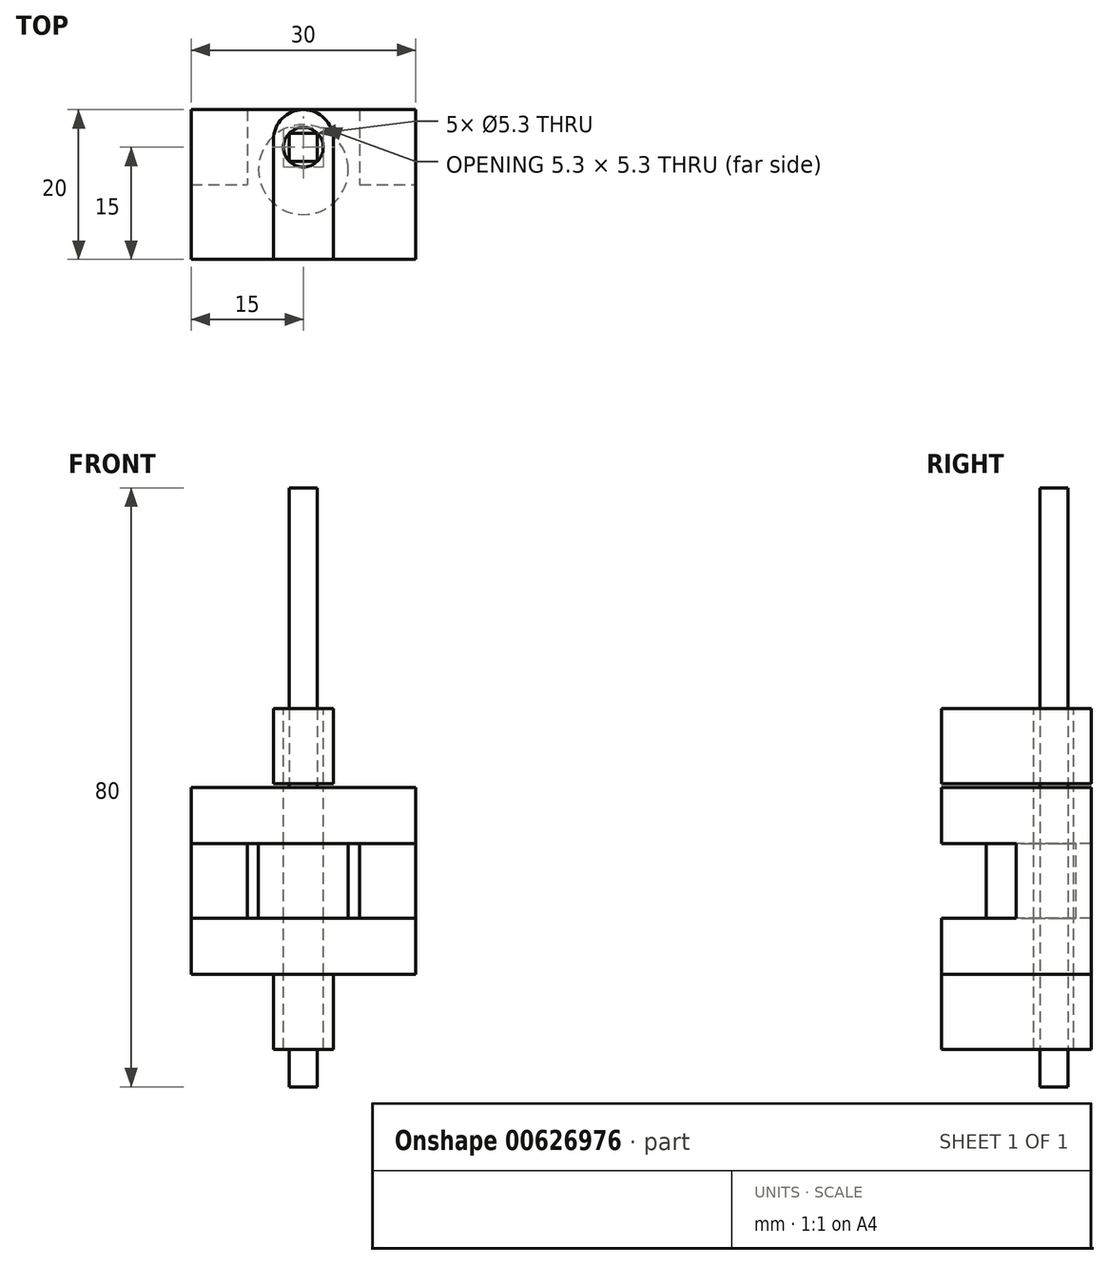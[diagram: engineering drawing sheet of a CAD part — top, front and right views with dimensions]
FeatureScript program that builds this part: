
annotation { "Feature Type Name" : "Feature", "Feature Type Description" : "" }
export const myFeature = defineFeature(function(context is Context, id is Id, definition is map)
    precondition{}
    {
        {
            var Q0;
            Q0=qCreatedBy(makeId("Top.planeOp"),FACE);
            var sketch = newSketch(context, id + "F0", { "sketchPlane" : qUnion([Q0])});
            skLineSegment(sketch, "E0.bottom", {"start": v(0, 0) * mm, "end": v(30, 0) * mm});
            skLineSegment(sketch, "E0.top", {"start": v(0, 20) * mm, "end": v(30, 20) * mm});
            skLineSegment(sketch, "E0.left", {"start": v(0, 0) * mm, "end": v(0, 20) * mm});
            skLineSegment(sketch, "E0.right", {"start": v(30, 0) * mm, "end": v(30, 20) * mm});
            skSolve(sketch);
        }
        {
            var Q0;
            Q0=makeQuery(id+"F0.imprint","IMPRINT",FACE,{"disambiguationData":[TD([[makeQuery(id+"F0.imprint","IMPRINT",EDGE,{"derivedFrom":sQuery(id+"F0.wireOp",EDGE,"E0.bottom")}),1.0]])]});
            extrude(context, id + "F1", {"entities" : qUnion([Q0]), "depth" : 25 * mm, "offsetDistance" : 25 * mm});
        }
        {
            var Q0;
            Q0=makeQuery(id+"F1.opExtrude","SWEPT_FACE",FACE,{"disambiguationData":[OSD([sQuery(id+"F0.wireOp",EDGE,"E0.bottom")])]});
            var sketch = newSketch(context, id + "F2", { "sketchPlane" : qUnion([Q0])});
            skLineSegment(sketch, "E1.bottom", {"start": v(0, 7.5) * mm, "end": v(30, 7.5) * mm});
            skLineSegment(sketch, "E1.top", {"start": v(0, 17.5) * mm, "end": v(30, 17.5) * mm});
            skLineSegment(sketch, "E1.left", {"start": v(0, 7.5) * mm, "end": v(0, 17.5) * mm});
            skLineSegment(sketch, "E1.right", {"start": v(30, 7.5) * mm, "end": v(30, 17.5) * mm});
            skLineSegment(sketch, "E2", {"start": v(20.4, 12.5) * mm, "end": v(0, 12.5) * mm, "construction": true});
            skSolve(sketch);
        }
        {
            var Q0;
            Q0=makeQuery(id+"F2.imprint","IMPRINT",FACE,{"disambiguationData":[TD([[makeQuery(id+"F2.imprint","IMPRINT",EDGE,{"derivedFrom":sQuery(id+"F2.wireOp",EDGE,"E1.bottom")}),1.0]])]});
            extrude(context, id + "F3", {"entities" : qUnion([Q0]), "operationType" : NewBodyOperationType.REMOVE, "oppositeDirection" : true, "depth" : 10 * mm, "offsetDistance" : 25 * mm});
        }
        {
            var Q0;
            Q0=makeQuery(id+"F3.boolean.opBoolean","COPY",FACE,{"derivedFrom":makeQuery(id+"F3.opExtrude","CAP_FACE",FACE,{"disambiguationData":[OSD([sQuery(id+"F2.wireOp",EDGE,"E1.bottom"),sQuery(id+"F2.wireOp",EDGE,"E1.top"),sQuery(id+"F2.wireOp",EDGE,"E1.left"),sQuery(id+"F2.wireOp",EDGE,"E1.right")])],"isStart":false})});
            var sketch = newSketch(context, id + "F4", { "sketchPlane" : qUnion([Q0])});
            skLineSegment(sketch, "E3.bottom", {"start": v(22.5, 17.5) * mm, "end": v(7.5, 17.5) * mm});
            skLineSegment(sketch, "E3.top", {"start": v(22.5, 7.5) * mm, "end": v(7.5, 7.5) * mm});
            skLineSegment(sketch, "E3.left", {"start": v(22.5, 17.5) * mm, "end": v(22.5, 7.5) * mm});
            skLineSegment(sketch, "E3.right", {"start": v(7.5, 17.5) * mm, "end": v(7.5, 7.5) * mm});
            skLineSegment(sketch, "E4", {"start": v(15, 17.5) * mm, "end": v(15, 7.5) * mm, "construction": true});
            skSolve(sketch);
        }
        {
            var Q0;
            Q0=makeQuery(id+"F4.imprint","IMPRINT",FACE,{"disambiguationData":[TD([[makeQuery(id+"F4.imprint","IMPRINT",EDGE,{"derivedFrom":sQuery(id+"F4.wireOp",EDGE,"E3.bottom")}),-1.0]])]});
            extrude(context, id + "F5", {"entities" : qUnion([Q0]), "operationType" : NewBodyOperationType.REMOVE, "endBound" : BoundingType.THROUGH_ALL, "oppositeDirection" : true, "depth" : 25 * mm, "offsetDistance" : 25 * mm});
        }
        {
            var Q0;
            Q0=makeQuery(id+"F5.boolean.opBoolean","MERGE",FACE,{"derivedFrom":[makeQuery(id+"F3.boolean.opBoolean","COPY",FACE,{"derivedFrom":makeQuery(id+"F3.opExtrude","SWEPT_FACE",FACE,{"disambiguationData":[OSD([sQuery(id+"F2.wireOp",EDGE,"E1.bottom")])]})}),makeQuery(id+"F5.opExtrude","SWEPT_FACE",FACE,{"disambiguationData":[OSD([sQuery(id+"F4.wireOp",EDGE,"E3.top")])]})]});
            var sketch = newSketch(context, id + "F6", { "sketchPlane" : qUnion([Q0])});
            skCircle(sketch, "E5", {"center": v(15, 15) * mm, "radius": 2.65 * mm});
            skLineSegment(sketch, "E6", {"start": v(15, 15) * mm, "end": v(15, 12.34) * mm, "construction": true});
            skSolve(sketch);
        }
        {
            var Q0;
            Q0=makeQuery(id+"F6.imprint","IMPRINT",FACE,{"disambiguationData":[TD([[makeQuery(id+"F6.imprint","IMPRINT",EDGE,{"derivedFrom":sQuery(id+"F6.wireOp",EDGE,"E5")}),1.0]])]});
            var Q1;
            Q1=sQuery(id+"F6.wireOp",EDGE,"E5");
            extrude(context, id + "F7", {"entities" : qUnion([Q0]), "operationType" : NewBodyOperationType.REMOVE, "surfaceEntities" : qUnion([Q1]), "endBound" : BoundingType.SYMMETRIC, "oppositeDirection" : true, "depth" : 50 * mm, "offsetDistance" : 25 * mm});
        }
        {
            var Q0;
            Q0=makeQuery(id+"F1.opExtrude","CAP_FACE",FACE,{"disambiguationData":[OSD([sQuery(id+"F0.wireOp",EDGE,"E0.bottom"),sQuery(id+"F0.wireOp",EDGE,"E0.top"),sQuery(id+"F0.wireOp",EDGE,"E0.left"),sQuery(id+"F0.wireOp",EDGE,"E0.right")])],"isStart":false});
            var sketch = newSketch(context, id + "F8", { "sketchPlane" : qUnion([Q0])});
            skLineSegment(sketch, "E7", {"start": v(15, 15) * mm, "end": v(15, 17.65) * mm, "construction": true});
            skLineSegment(sketch, "E8.bottom", {"start": v(16.87, 13.13) * mm, "end": v(13.13, 13.13) * mm});
            skLineSegment(sketch, "E8.top", {"start": v(16.87, 16.87) * mm, "end": v(13.13, 16.87) * mm});
            skLineSegment(sketch, "E8.left", {"start": v(16.87, 13.13) * mm, "end": v(16.87, 16.87) * mm});
            skLineSegment(sketch, "E8.right", {"start": v(13.13, 13.13) * mm, "end": v(13.13, 16.87) * mm});
            skSolve(sketch);
        }
        {
            var Q0;
            Q0=makeQuery(id+"F8.imprint","IMPRINT",FACE,{"disambiguationData":[TD([[makeQuery(id+"F8.imprint","IMPRINT",EDGE,{"derivedFrom":sQuery(id+"F8.wireOp",EDGE,"E8.bottom")}),-1.0]])]});
            extrude(context, id + "F9", {"entities" : qUnion([Q0]), "endBound" : BoundingType.SYMMETRIC, "depth" : 80 * mm, "offsetDistance" : 25 * mm});
        }
        {
            var Q0;
            Q0=makeQuery(id+"F5.boolean.opBoolean","MERGE",FACE,{"derivedFrom":[makeQuery(id+"F3.boolean.opBoolean","COPY",FACE,{"derivedFrom":makeQuery(id+"F3.opExtrude","SWEPT_FACE",FACE,{"disambiguationData":[OSD([sQuery(id+"F2.wireOp",EDGE,"E1.top")])]})}),makeQuery(id+"F5.opExtrude","SWEPT_FACE",FACE,{"disambiguationData":[OSD([sQuery(id+"F4.wireOp",EDGE,"E3.bottom")])]})]});
            var sketch = newSketch(context, id + "F10", { "sketchPlane" : qUnion([Q0])});
            skCircle(sketch, "E9", {"center": v(15, -12) * mm, "radius": 6 * mm});
            skLineSegment(sketch, "E10", {"start": v(15.06, -12.35) * mm, "end": v(15, -15) * mm, "construction": true});
            skLineSegment(sketch, "E11", {"start": v(15, -15) * mm, "end": v(15, -12) * mm, "construction": true});
            skSolve(sketch);
        }
        {
            var Q0;
            Q0=makeQuery(id+"F10.imprint","IMPRINT",FACE,{"disambiguationData":[TD([[makeQuery(id+"F10.imprint","IMPRINT",EDGE,{"derivedFrom":sQuery(id+"F10.wireOp",EDGE,"E9")}),1.0]])]});
            var Q1;
            Q1=sQuery(id+"F10.wireOp",EDGE,"E9");
            var Q2;
            Q2=makeQuery(id+"F5.boolean.opBoolean","MERGE",FACE,{"derivedFrom":[makeQuery(id+"F3.boolean.opBoolean","COPY",FACE,{"derivedFrom":makeQuery(id+"F3.opExtrude","SWEPT_FACE",FACE,{"disambiguationData":[OSD([sQuery(id+"F2.wireOp",EDGE,"E1.bottom")])]})}),makeQuery(id+"F5.opExtrude","SWEPT_FACE",FACE,{"disambiguationData":[OSD([sQuery(id+"F4.wireOp",EDGE,"E3.top")])]})]});
            extrude(context, id + "F11", {"entities" : qUnion([Q0]), "surfaceEntities" : qUnion([Q1]), "endBound" : BoundingType.UP_TO_SURFACE, "depth" : 25 * mm, "endBoundEntityFace" : qUnion([Q2]), "offsetDistance" : 25 * mm});
        }
        {
            var Q0;
            Q0=makeQuery(id+"F1.opExtrude","CAP_FACE",FACE,{"disambiguationData":[OSD([sQuery(id+"F0.wireOp",EDGE,"E0.bottom"),sQuery(id+"F0.wireOp",EDGE,"E0.top"),sQuery(id+"F0.wireOp",EDGE,"E0.left"),sQuery(id+"F0.wireOp",EDGE,"E0.right")])],"isStart":true});
            var sketch = newSketch(context, id + "F12", { "sketchPlane" : qUnion([Q0])});
            skLineSegment(sketch, "E12.top", {"start": v(19, 0) * mm, "end": v(11, 0) * mm});
            skLineSegment(sketch, "E12.left", {"start": v(19, -16) * mm, "end": v(19, 0) * mm});
            skLineSegment(sketch, "E12.right", {"start": v(11, -16) * mm, "end": v(11, 0) * mm});
            skArc(sketch, "E13", {"start": v(11, -16) * mm, "mid": v(15, -20) * mm, "end": v(19, -16) * mm});
            skLineSegment(sketch, "E14", {"start": v(15, -15) * mm, "end": v(15, -20) * mm, "construction": true});
            skSolve(sketch);
        }
        {
            var Q0;
            Q0=makeQuery(id+"F12.imprint","IMPRINT",FACE,{"disambiguationData":[TD([[makeQuery(id+"F12.imprint","IMPRINT",EDGE,{"derivedFrom":sQuery(id+"F12.wireOp",EDGE,"E12.top")}),-1.0]])]});
            extrude(context, id + "F13", {"entities" : qUnion([Q0]), "depth" : 10 * mm, "offsetDistance" : 25 * mm});
        }
        {
            var Q0;
            Q0=makeQuery(id+"F13.opExtrude","SWEPT_BODY",BODY,{"disambiguationData":[OSD([sQuery(id+"F0.wireOp",EDGE,"E0.bottom"),sQuery(id+"F0.wireOp",EDGE,"E0.top"),sQuery(id+"F0.wireOp",EDGE,"E0.left"),sQuery(id+"F0.wireOp",EDGE,"E0.right"),sQuery(id+"F6.wireOp",EDGE,"E5"),sQuery(id+"F12.wireOp",EDGE,"E12.top"),sQuery(id+"F12.wireOp",EDGE,"E12.left"),sQuery(id+"F12.wireOp",EDGE,"E12.right"),sQuery(id+"F12.wireOp",EDGE,"E13")])]});
            transform(context, id + "F14", {"entities" : qUnion([Q0]), "transformType" : TransformType.TRANSLATION_3D, "dx" : 0 * mm, "dy" : 0 * mm, "dz" : 35.5 * mm, "makeCopy" : true});
        }
    });
